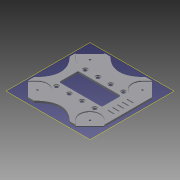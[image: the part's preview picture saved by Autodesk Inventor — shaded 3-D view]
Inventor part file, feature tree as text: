
AUTODESK INVENTOR PART (.ipt)
format: ipt  version: 2015 (Build 190159000, 159)  size: 262,656 bytes
history: native  units: mm
features: sketch x9, extrude x7, mirror x5, hole x2, pattern_linear x2, split x1, plane x1, chamfer x1, fillet x1
ambient origin geometry x8: Origin, YZ Plane, XZ Plane, XY Plane, X Axis, Y Axis, Z Axis, Center Point
bodies: Solid1 (feature_tree)
feature tree (29):
  extrude  "Extrusion1"  Depth=160.0mm
  split  "Split1"
  mirror  "Mirror1"
  mirror  "Mirror2"
  extrude  "Extrusion2"  TaperAngle=45.0deg  [1 undecoded]
  hole  "Hole1"  [1 undecoded]
  mirror  "Mirror3"
  mirror  "Mirror4"
  extrude  "Extrusion3"  Depth=10.0mm
  hole  "Hole2"  [1 undecoded]
  extrude  "Extrusion4"  Depth=10.0mm TaperAngle=0.0deg
  extrude  "Extrusion5"  Depth=10.0mm TaperAngle=0.0deg
  mirror  "Mirror8"
  plane  "Work Plane1"
  chamfer  "Chamfer5"  Distance=10.0mm
  extrude  "Extrusion7"  Depth=3.0mm
  pattern_linear  "Rectangular Pattern1"  Spacing1=9.0mm  [1 undecoded]
  pattern_linear  "Rectangular Pattern2"  Spacing1=9.0mm  [1 undecoded]
  extrude  "Extrusion8"  Depth=3.0mm TaperAngle=45.0deg
  fillet  "Fillet1"  Radius=1.0mm
  sketch  "Sketch2"  dims[d0=160.0mm d1=160.0mm]
  sketch  "Sketch3"  dims[d2=4.0mm d3=0.0mm d4=45.0deg]
  sketch  "Sketch4"  dims[d5=30.0mm d7=2.0mm d8=0.0mm]
  sketch  "Sketch5"  dims[d9=4.0mm]
  sketch  "Sketch6"  dims[d10=4.0mm d11=6.0mm d12=4.0mm d13=2.0mm d14=90.0deg d15=8.0mm d16=20.594885mm d17=10.0mm]
  sketch  "Sketch7"  dims[d18=30.0mm d19=40.0mm]
  sketch  "Sketch9"  dims[d20=10.0mm d21=1.5mm d22=0.0mm]
  sketch  "Sketch11"  dims[d23=10.0mm d24=10.0mm]
  sketch  "Sketch12"  dims[d25=7.0mm d26=6.0mm d27=4.0mm d28=2.0mm d29=90.0deg d30=8.0mm d31=20.594885mm d42=10.0mm d43=0.0mm d46=10.0mm d47=0.0mm d50=9.0mm d51=9.0mm d52=9.0mm d56=0.5mm d57=2.0mm d58=45.0deg d59=1.0mm d60=10.0mm d61=10.0mm d62=0.0mm d63=50.0mm d65=10.0mm d66=40.0mm d68=-80.0mm d69=20.0mm d71=60.0mm d72=90.0mm d73=40.0mm d74=10.0mm d75=0.0mm d76=3.0mm]
note: 5 required parameter values undecoded (feature->parameter linkage not recoverable at this tier; creation-order binding heuristic only, values carry confidence <= 0.55)
